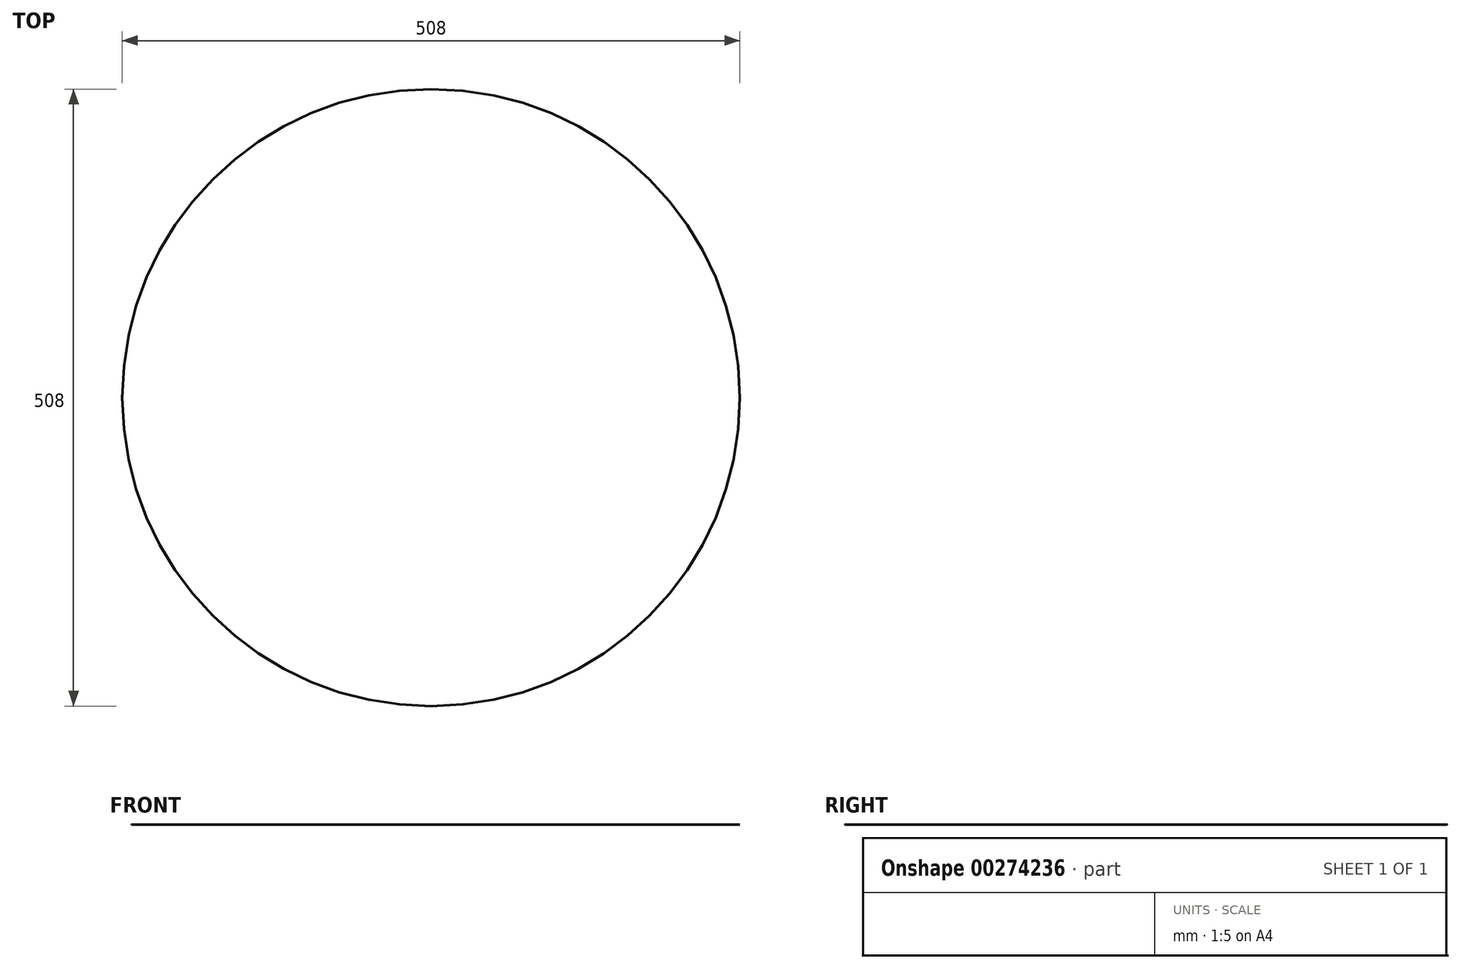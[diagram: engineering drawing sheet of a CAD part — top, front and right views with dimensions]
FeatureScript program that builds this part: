
annotation { "Feature Type Name" : "Feature", "Feature Type Description" : "" }
export const myFeature = defineFeature(function(context is Context, id is Id, definition is map)
    precondition{}
    {
        {
            var Q0;
            Q0=qCreatedBy(makeId("Front.planeOp"),FACE);
            var sketch = newSketch(context, id + "F0", { "sketchPlane" : qUnion([Q0])});
            skLineSegment(sketch, "E0.bottom", {"start": v(254, 0) * mm, "end": v(254, 0) * mm});
            skLineSegment(sketch, "E0.top", {"start": v(0, 254) * mm, "end": v(254, 254) * mm});
            skLineSegment(sketch, "E0.left", {"start": v(0, 254) * mm, "end": v(0, 254) * mm});
            skLineSegment(sketch, "E0.right", {"start": v(254, 0) * mm, "end": v(254, 254) * mm});
            skPoint(sketch, "E1.visualSharp", {"position": v(0, 0) * mm});
            skArc(sketch, "E1.filletArc", {"start": v(0, 254) * mm, "mid": v(74.4, 74.4) * mm, "end": v(254, 0) * mm});
            skLineSegment(sketch, "E2.top", {"start": v(0, 0) * mm, "end": v(254, 0) * mm});
            skLineSegment(sketch, "E2.left", {"start": v(0, 254) * mm, "end": v(0, 0) * mm});
            skLineSegment(sketch, "E2.right", {"start": v(254, 254) * mm, "end": v(254, 0) * mm});
            skSolve(sketch);
        }
        {
            var Q0;
            {var subQ0=sQuery(id+"F0.wireOp",EDGE,"E1.filletArc");Q0=makeQuery(id+"F0.imprint","IMPRINT",FACE,{"disambiguationData":[TD([[makeQuery(id+"F0.imprint","IMPRINT",EDGE,{"derivedFrom":subQ0}),-1.0]])]});}
            var Q1;
            Q1=sQuery(id+"F0.wireOp",EDGE,"E2.left");
            revolve(context, id + "F1", {"entities" : qUnion([Q0]), "axis" : qUnion([Q1]), "revolveType" : RevolveType.FULL});
        }
    });
